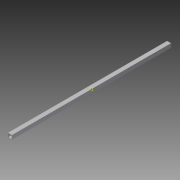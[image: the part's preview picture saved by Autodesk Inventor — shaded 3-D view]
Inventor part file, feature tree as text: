
AUTODESK INVENTOR PART (.ipt)
format: ipt  version: 2013 (Build 170138000, 138)  size: 76,800 bytes
history: native  units: in
note: dims shown in document units (in); Inventor stores cm internally (conversion verified against a paired STEP export)
features: other x3, sketch x1, plane x1
ambient origin geometry x8: Origin, YZ Plane, XZ Plane, XY Plane, X Axis, Y Axis, Z Axis, Center Point
bodies: Solid1 (feature_tree)
feature tree (5):
  other  "FE-00036Support.ipt"
  other  "Solid1::FE-00036Support.ipt"
  other  "TaggingFeature1"
  sketch  "Sketch1"  dims[d0=0.3937in d1=0.0in]
  plane  "Work Plane1"
